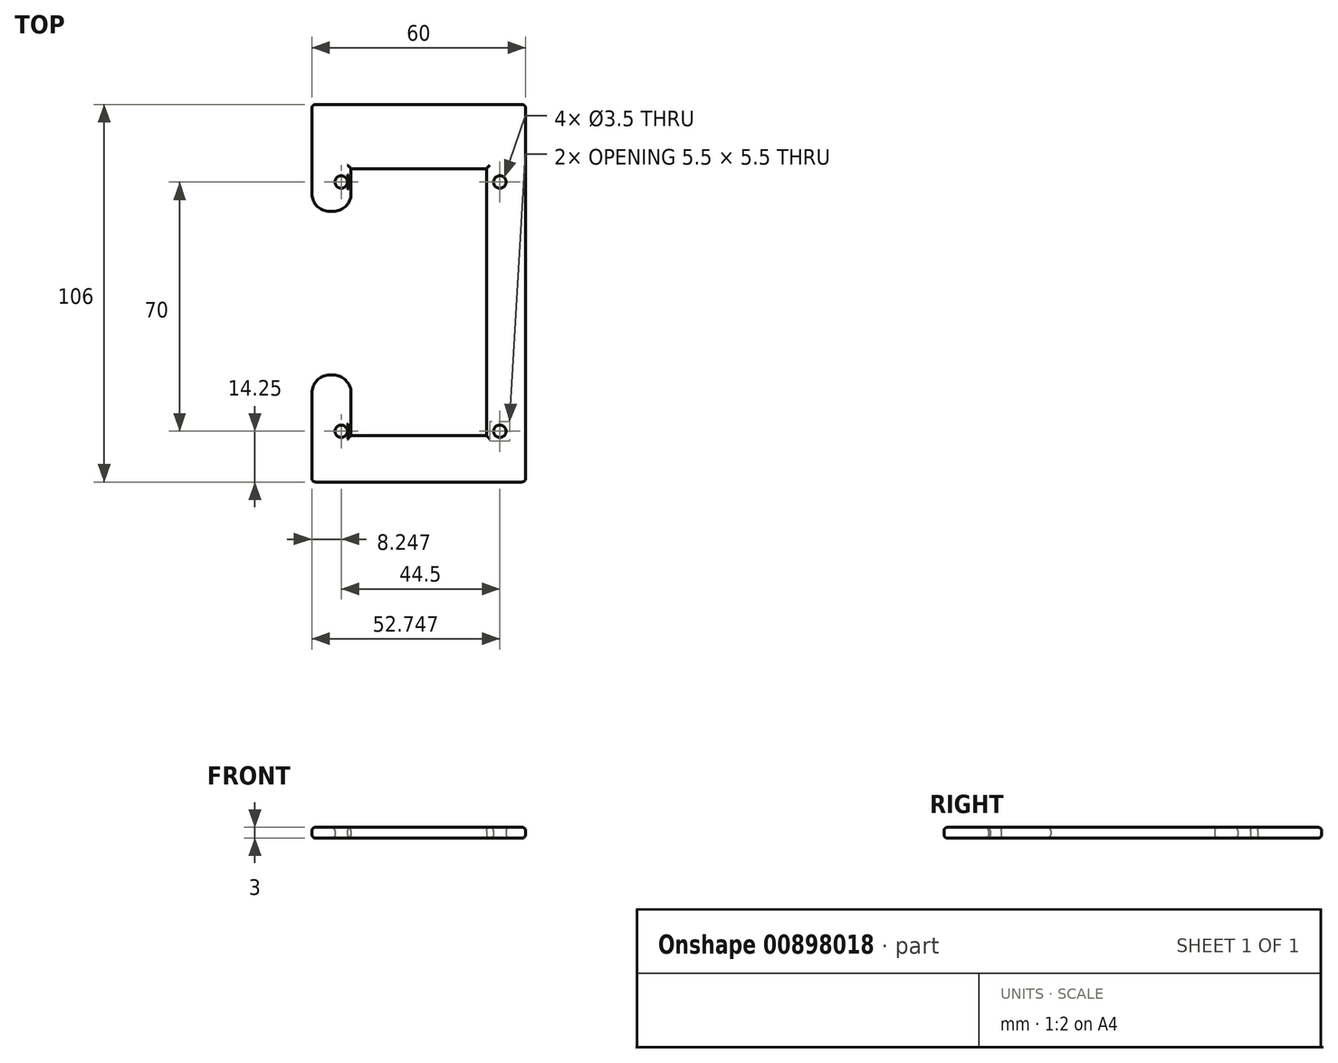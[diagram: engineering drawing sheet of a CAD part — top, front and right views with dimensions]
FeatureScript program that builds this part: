
annotation { "Feature Type Name" : "Feature", "Feature Type Description" : "" }
export const myFeature = defineFeature(function(context is Context, id is Id, definition is map)
    precondition{}
    {
        {
            var Q0;
            Q0=qCreatedBy(makeId("Top.planeOp"),FACE);
            var sketch = newSketch(context, id + "F0", { "sketchPlane" : qUnion([Q0])});
            skLineSegment(sketch, "E0.top", {"start": v(-20.8, -33) * mm, "end": v(17.2, -33) * mm});
            skLineSegment(sketch, "E0.left", {"start": v(-26.8, 40) * mm, "end": v(-26.8, 30) * mm, "construction": true});
            skLineSegment(sketch, "E0.right", {"start": v(23.2, 42) * mm, "end": v(23.2, -33) * mm, "construction": true});
            skCircle(sketch, "E1", {"center": v(20.95, 38.25) * mm, "radius": 1.75 * mm});
            skCircle(sketch, "E2", {"center": v(20.95, -31.75) * mm, "radius": 1.75 * mm});
            skCircle(sketch, "E3", {"center": v(-23.55, -31.75) * mm, "radius": 1.75 * mm});
            skCircle(sketch, "E4", {"center": v(-23.55, 38.25) * mm, "radius": 1.75 * mm});
            skLineSegment(sketch, "E5.right", {"start": v(17.2, 34) * mm, "end": v(17.2, -29) * mm});
            skLineSegment(sketch, "E6", {"start": v(-20.8, -29) * mm, "end": v(-20.8, -33) * mm});
            skLineSegment(sketch, "E7", {"start": v(17.2, -29) * mm, "end": v(17.2, -33) * mm});
            skLineSegment(sketch, "E8", {"start": v(17.2, 34) * mm, "end": v(17.2, 47) * mm});
            skLineSegment(sketch, "E9", {"start": v(-26.8, -33) * mm, "end": v(-26.8, -46) * mm, "construction": true});
            skLineSegment(sketch, "E10", {"start": v(-26.8, -46) * mm, "end": v(23.2, -46) * mm});
            skLineSegment(sketch, "E11", {"start": v(23.2, -46) * mm, "end": v(23.2, -33) * mm, "construction": true});
            skLineSegment(sketch, "E12", {"start": v(-26.8, 40) * mm, "end": v(-26.8, 60) * mm, "construction": true});
            skLineSegment(sketch, "E13", {"start": v(-26.8, 60) * mm, "end": v(23.2, 60) * mm});
            skLineSegment(sketch, "E14", {"start": v(-20.8, 47) * mm, "end": v(17.2, 47) * mm});
            skLineSegment(sketch, "E15", {"start": v(23.2, 60) * mm, "end": v(28.2, 60) * mm});
            skLineSegment(sketch, "E16", {"start": v(28.2, 60) * mm, "end": v(28.2, -46) * mm});
            skLineSegment(sketch, "E17", {"start": v(28.2, -46) * mm, "end": v(23.2, -46) * mm});
            skLineSegment(sketch, "E18", {"start": v(-26.8, 60) * mm, "end": v(-31.8, 60) * mm});
            skLineSegment(sketch, "E19", {"start": v(-31.8, 60) * mm, "end": v(-31.8, 35) * mm});
            skLineSegment(sketch, "E20", {"start": v(-31.8, -46) * mm, "end": v(-26.8, -46) * mm});
            skLineSegment(sketch, "E21", {"start": v(-26.8, 30) * mm, "end": v(-25.8, 30) * mm});
            skLineSegment(sketch, "E22", {"start": v(-26.8, -16) * mm, "end": v(-25.8, -16) * mm});
            skLineSegment(sketch, "E23.trimOffspring", {"start": v(-20.8, -21) * mm, "end": v(-20.8, -29) * mm});
            skLineSegment(sketch, "E24.trimOffspring", {"start": v(-31.8, -21) * mm, "end": v(-31.8, -46) * mm});
            skLineSegment(sketch, "E25.trimOffspring", {"start": v(-26.8, -16) * mm, "end": v(-26.8, -33) * mm, "construction": true});
            skPoint(sketch, "E26.visualSharp", {"position": v(-31.8, 30) * mm});
            skArc(sketch, "E26.filletArc", {"start": v(-31.8, 35) * mm, "mid": v(-30.34, 31.46) * mm, "end": v(-26.8, 30) * mm});
            skPoint(sketch, "E27.visualSharp", {"position": v(-31.8, -16) * mm});
            skArc(sketch, "E27.filletArc", {"start": v(-26.8, -16) * mm, "mid": v(-30.34, -17.46) * mm, "end": v(-31.8, -21) * mm});
            skPoint(sketch, "E28.visualSharp", {"position": v(-20.8, -16) * mm});
            skArc(sketch, "E28.filletArc", {"start": v(-20.8, -21) * mm, "mid": v(-22.27, -17.46) * mm, "end": v(-25.8, -16) * mm});
            skLineSegment(sketch, "E29", {"start": v(-20.8, 35) * mm, "end": v(-20.8, 47) * mm});
            skPoint(sketch, "E30.visualSharp", {"position": v(-20.8, 30) * mm});
            skArc(sketch, "E30.filletArc", {"start": v(-25.8, 30) * mm, "mid": v(-22.27, 31.46) * mm, "end": v(-20.8, 35) * mm});
            skLineSegment(sketch, "E31.trimOffspring", {"start": v(-20.8, 42) * mm, "end": v(17.2, 42) * mm});
            skSolve(sketch);
        }
        {
            var Q0;
            Q0=makeQuery(id+"F0.imprint","IMPRINT",FACE,{"disambiguationData":[TD([[makeQuery(id+"F0.imprint","IMPRINT",EDGE,{"derivedFrom":sQuery(id+"F0.wireOp",EDGE,"E0.top")}),-1.0]])]});
            var Q1;
            Q1 = qSketchRegion(id + "F0", true);
            extrude(context, id + "F1", {"entities" : qUnion([Q0, Q1]), "depth" : 3 * mm, "offsetDistance" : 25 * mm});
        }
        {
            var Q0;
            Q0=makeQuery(id+"F1.opExtrude","CAP_FACE",FACE,{"disambiguationData":[OSD([sQuery(id+"F0.wireOp",EDGE,"E0.top"),sQuery(id+"F0.wireOp",EDGE,"E0.left"),sQuery(id+"F0.wireOp",EDGE,"E0.right"),sQuery(id+"F0.wireOp",EDGE,"E1"),sQuery(id+"F0.wireOp",EDGE,"E2"),sQuery(id+"F0.wireOp",EDGE,"E3"),sQuery(id+"F0.wireOp",EDGE,"E4"),sQuery(id+"F0.wireOp",EDGE,"E5.left"),sQuery(id+"F0.wireOp",EDGE,"E5.right"),sQuery(id+"F0.wireOp",EDGE,"E6"),sQuery(id+"F0.wireOp",EDGE,"E7"),sQuery(id+"F0.wireOp",EDGE,"AvtgV1NG-GVge-MWpO-kYc9-HvFemwJbZgIj"),sQuery(id+"F0.wireOp",EDGE,"E8"),sQuery(id+"F0.wireOp",EDGE,"E9"),sQuery(id+"F0.wireOp",EDGE,"E10"),sQuery(id+"F0.wireOp",EDGE,"E11"),sQuery(id+"F0.wireOp",EDGE,"E12"),sQuery(id+"F0.wireOp",EDGE,"E13"),sQuery(id+"F0.wireOp",EDGE,"XwiBSKKJ-Dpwt-UDFX-hsP3-0yti6UOtJj1k"),sQuery(id+"F0.wireOp",EDGE,"E14")])],"isStart":false});
            var Q1;
            Q1=makeQuery(id+"F1.opExtrude","CAP_FACE",FACE,{"disambiguationData":[OSD([sQuery(id+"F0.wireOp",EDGE,"E0.top"),sQuery(id+"F0.wireOp",EDGE,"E0.left"),sQuery(id+"F0.wireOp",EDGE,"E0.right"),sQuery(id+"F0.wireOp",EDGE,"E1"),sQuery(id+"F0.wireOp",EDGE,"E2"),sQuery(id+"F0.wireOp",EDGE,"E3"),sQuery(id+"F0.wireOp",EDGE,"E4"),sQuery(id+"F0.wireOp",EDGE,"E5.left"),sQuery(id+"F0.wireOp",EDGE,"E5.right"),sQuery(id+"F0.wireOp",EDGE,"E6"),sQuery(id+"F0.wireOp",EDGE,"E7"),sQuery(id+"F0.wireOp",EDGE,"AvtgV1NG-GVge-MWpO-kYc9-HvFemwJbZgIj"),sQuery(id+"F0.wireOp",EDGE,"E8"),sQuery(id+"F0.wireOp",EDGE,"E9"),sQuery(id+"F0.wireOp",EDGE,"E10"),sQuery(id+"F0.wireOp",EDGE,"E11"),sQuery(id+"F0.wireOp",EDGE,"E12"),sQuery(id+"F0.wireOp",EDGE,"E13"),sQuery(id+"F0.wireOp",EDGE,"XwiBSKKJ-Dpwt-UDFX-hsP3-0yti6UOtJj1k"),sQuery(id+"F0.wireOp",EDGE,"E14")])],"isStart":true});
            var Q2;
            Q2=makeQuery(id+"F1.opExtrude","SWEPT_FACE",FACE,{"disambiguationData":[OSD([sQuery(id+"F0.wireOp",EDGE,"E0.right"),sQuery(id+"F0.wireOp",EDGE,"E11"),sQuery(id+"F0.wireOp",EDGE,"XwiBSKKJ-Dpwt-UDFX-hsP3-0yti6UOtJj1k")])]});
            var Q3;
            Q3=makeQuery(id+"F1.opExtrude","SWEPT_FACE",FACE,{"disambiguationData":[OSD([sQuery(id+"F0.wireOp",EDGE,"E13")])]});
            var Q4;
            Q4=makeQuery(id+"F1.opExtrude","SWEPT_FACE",FACE,{"disambiguationData":[OSD([sQuery(id+"F0.wireOp",EDGE,"E0.left"),sQuery(id+"F0.wireOp",EDGE,"E9"),sQuery(id+"F0.wireOp",EDGE,"E12")])]});
            var Q5;
            Q5=makeQuery(id+"F1.opExtrude","SWEPT_FACE",FACE,{"disambiguationData":[OSD([sQuery(id+"F0.wireOp",EDGE,"E10")])]});
            fillet(context, id + "F2", {"entities" : qUnion([Q0, Q1, Q2, Q3, Q4, Q5]), "radius" : 1 * mm, "tangentPropagation" : true, "allowEdgeOverflow" : false});
        }
    });
